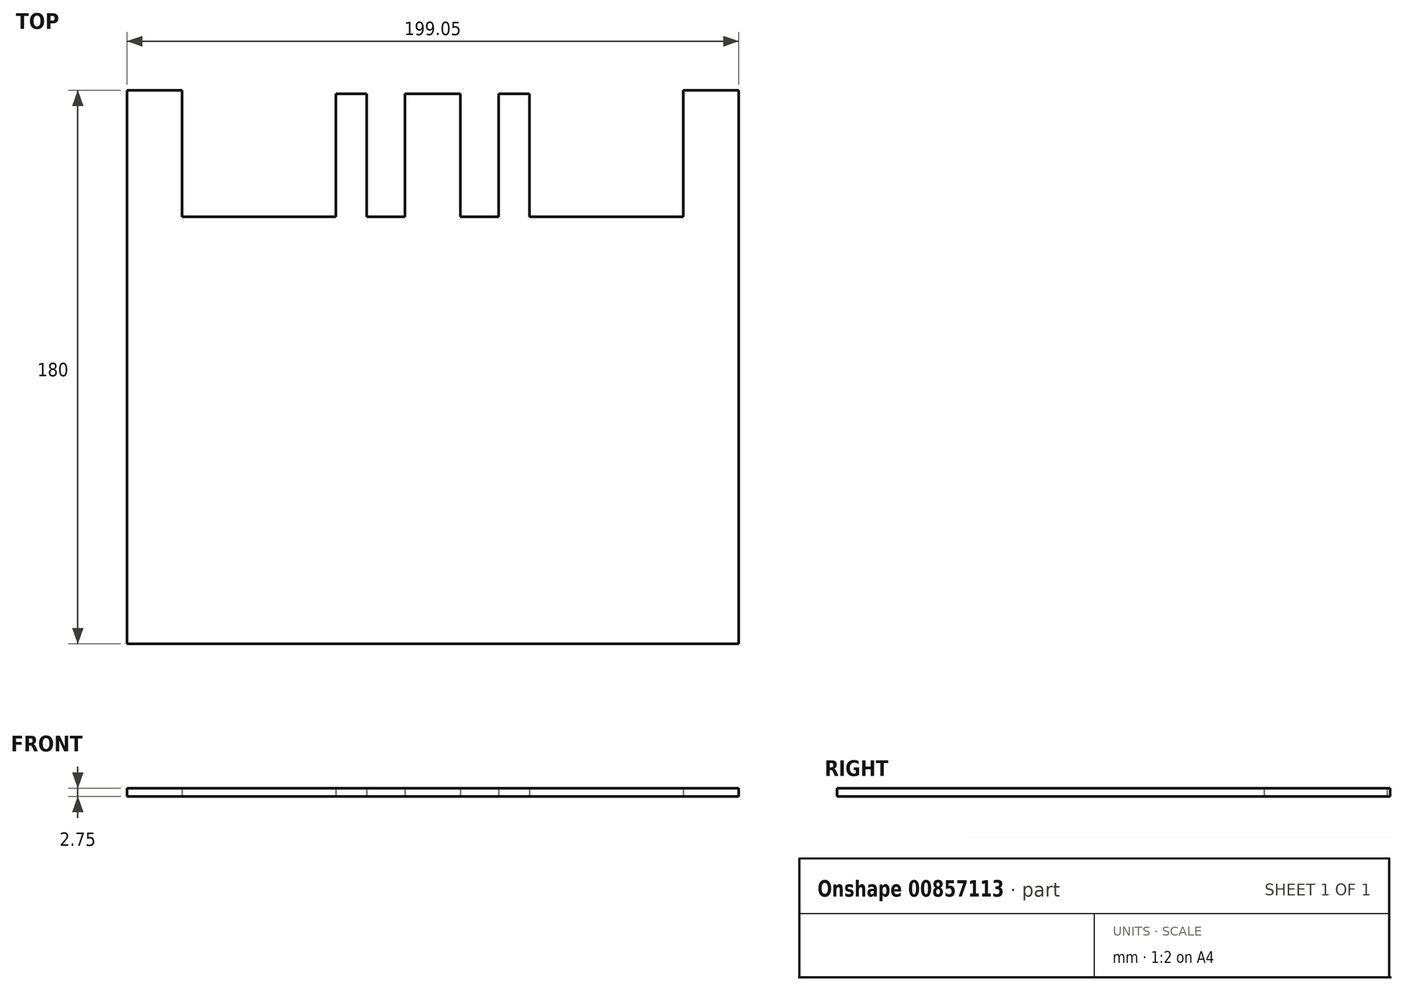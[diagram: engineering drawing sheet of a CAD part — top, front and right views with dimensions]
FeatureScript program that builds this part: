
annotation { "Feature Type Name" : "Feature", "Feature Type Description" : "" }
export const myFeature = defineFeature(function(context is Context, id is Id, definition is map)
    precondition{}
    {
        {
            var Q0;
            Q0=qCreatedBy(makeId("Top.planeOp"),FACE);
            var sketch = newSketch(context, id + "F0", { "sketchPlane" : qUnion([Q0])});
            skLineSegment(sketch, "E0", {"start": v(37.8, 21.87) * mm, "end": v(55.8, 21.87) * mm});
            skLineSegment(sketch, "E1", {"start": v(55.8, 21.87) * mm, "end": v(55.8, -18.13) * mm});
            skLineSegment(sketch, "E2", {"start": v(55.8, -18.13) * mm, "end": v(68.3, -18.13) * mm});
            skLineSegment(sketch, "E3", {"start": v(68.3, -18.13) * mm, "end": v(68.3, 21.87) * mm});
            skLineSegment(sketch, "E4", {"start": v(68.3, 21.87) * mm, "end": v(78.3, 21.87) * mm});
            skLineSegment(sketch, "E5", {"start": v(78.3, 21.87) * mm, "end": v(78.3, -18.13) * mm});
            skLineSegment(sketch, "E6", {"start": v(78.3, -18.13) * mm, "end": v(128.3, -18.13) * mm});
            skLineSegment(sketch, "E7", {"start": v(37.8, 21.87) * mm, "end": v(37.8, -18.13) * mm});
            skLineSegment(sketch, "E8", {"start": v(37.8, -18.13) * mm, "end": v(25.3, -18.13) * mm});
            skLineSegment(sketch, "E9", {"start": v(25.3, -18.13) * mm, "end": v(25.3, 21.87) * mm});
            skLineSegment(sketch, "E10", {"start": v(25.3, 21.87) * mm, "end": v(15.3, 21.87) * mm});
            skLineSegment(sketch, "E11", {"start": v(15.3, 21.87) * mm, "end": v(15.3, -18.13) * mm});
            skLineSegment(sketch, "E12", {"start": v(15.3, -18.13) * mm, "end": v(-34.7, -18.13) * mm});
            skLineSegment(sketch, "E13", {"start": v(-34.7, -18.13) * mm, "end": v(-34.7, 22.92) * mm});
            skLineSegment(sketch, "E14", {"start": v(-34.7, 22.92) * mm, "end": v(-52.7, 22.92) * mm});
            skLineSegment(sketch, "E15", {"start": v(-52.7, 22.92) * mm, "end": v(-52.7, -157.08) * mm});
            skLineSegment(sketch, "E16", {"start": v(-52.7, -157.08) * mm, "end": v(146.36, -157.08) * mm});
            skLineSegment(sketch, "E17", {"start": v(146.36, -157.08) * mm, "end": v(146.36, 22.92) * mm});
            skLineSegment(sketch, "E18", {"start": v(146.36, 22.92) * mm, "end": v(128.36, 22.92) * mm});
            skLineSegment(sketch, "E19", {"start": v(128.36, 22.92) * mm, "end": v(128.3, -18.13) * mm});
            skSolve(sketch);
        }
        {
            var Q0;
            Q0=makeQuery(id+"F0.imprint","IMPRINT",FACE,{"disambiguationData":[TD([[makeQuery(id+"F0.imprint","IMPRINT",EDGE,{"derivedFrom":sQuery(id+"F0.wireOp",EDGE,"E0")}),-1.0]])]});
            extrude(context, id + "F1", {"entities" : qUnion([Q0]), "depth" : 2.75 * mm, "offsetDistance" : 25 * mm});
        }
    });
